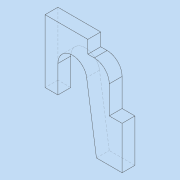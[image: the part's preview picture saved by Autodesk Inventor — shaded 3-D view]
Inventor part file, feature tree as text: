
AUTODESK INVENTOR PART (.ipt)
format: ipt  version: 2020 (Build 240168000, 168)  size: 107,008 bytes
history: native  units: mm
features: other x1, extrude x1
ambient origin geometry x8: Origin, YZ Plane, XZ Plane, XY Plane, X Axis, Y Axis, Z Axis, Center Point
bodies: Body1 (feature_tree)
feature tree (2):
  other  "實體1"
  extrude  "擠出1"  Depth=2.0mm
